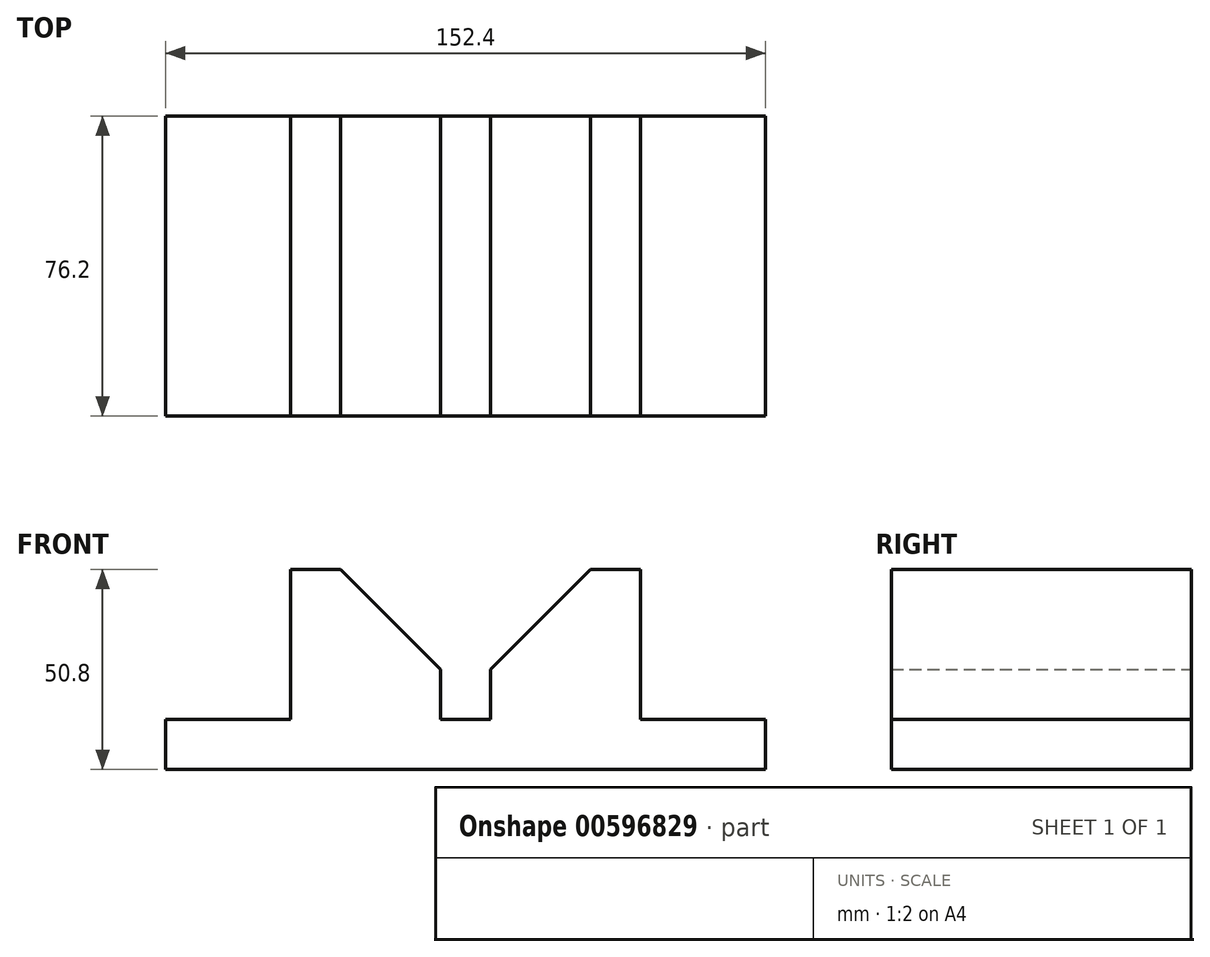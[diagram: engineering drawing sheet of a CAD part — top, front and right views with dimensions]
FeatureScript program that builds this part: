
annotation { "Feature Type Name" : "Feature", "Feature Type Description" : "" }
export const myFeature = defineFeature(function(context is Context, id is Id, definition is map)
    precondition{}
    {
        {
            var Q0;
            Q0=qCreatedBy(makeId("Front.planeOp"),FACE);
            var sketch = newSketch(context, id + "F0", { "sketchPlane" : qUnion([Q0])});
            skLineSegment(sketch, "E0", {"start": v(0, 0) * mm, "end": v(0, 12.7) * mm});
            skLineSegment(sketch, "E1", {"start": v(0, 12.7) * mm, "end": v(31.75, 12.7) * mm});
            skLineSegment(sketch, "E2", {"start": v(31.75, 12.7) * mm, "end": v(31.75, 50.8) * mm});
            skLineSegment(sketch, "E3", {"start": v(31.75, 50.8) * mm, "end": v(44.45, 50.8) * mm});
            skLineSegment(sketch, "E4", {"start": v(152.4, 0) * mm, "end": v(0, 0) * mm});
            skLineSegment(sketch, "E5", {"start": v(152.4, 0) * mm, "end": v(152.4, 12.7) * mm});
            skLineSegment(sketch, "E6", {"start": v(152.4, 12.7) * mm, "end": v(120.65, 12.7) * mm});
            skLineSegment(sketch, "E7", {"start": v(120.65, 12.7) * mm, "end": v(120.65, 50.8) * mm});
            skLineSegment(sketch, "E8", {"start": v(120.65, 50.8) * mm, "end": v(107.95, 50.8) * mm});
            skLineSegment(sketch, "E9", {"start": v(44.45, 50.8) * mm, "end": v(69.85, 25.4) * mm});
            skLineSegment(sketch, "E10", {"start": v(69.85, 25.4) * mm, "end": v(69.85, 12.7) * mm});
            skLineSegment(sketch, "E11", {"start": v(69.85, 12.7) * mm, "end": v(82.55, 12.7) * mm});
            skLineSegment(sketch, "E12", {"start": v(82.55, 12.7) * mm, "end": v(82.55, 25.4) * mm});
            skLineSegment(sketch, "E13", {"start": v(82.55, 25.4) * mm, "end": v(107.95, 50.8) * mm});
            skSolve(sketch);
        }
        {
            var Q0;
            Q0=makeQuery(id+"F0.imprint","IMPRINT",FACE,{"disambiguationData":[TD([[makeQuery(id+"F0.imprint","IMPRINT",EDGE,{"derivedFrom":sQuery(id+"F0.wireOp",EDGE,"E0")}),-1.0]])]});
            extrude(context, id + "F1", {"entities" : qUnion([Q0]), "depth" : 76.2 * mm, "offsetDistance" : 25.4 * mm});
        }
    });
